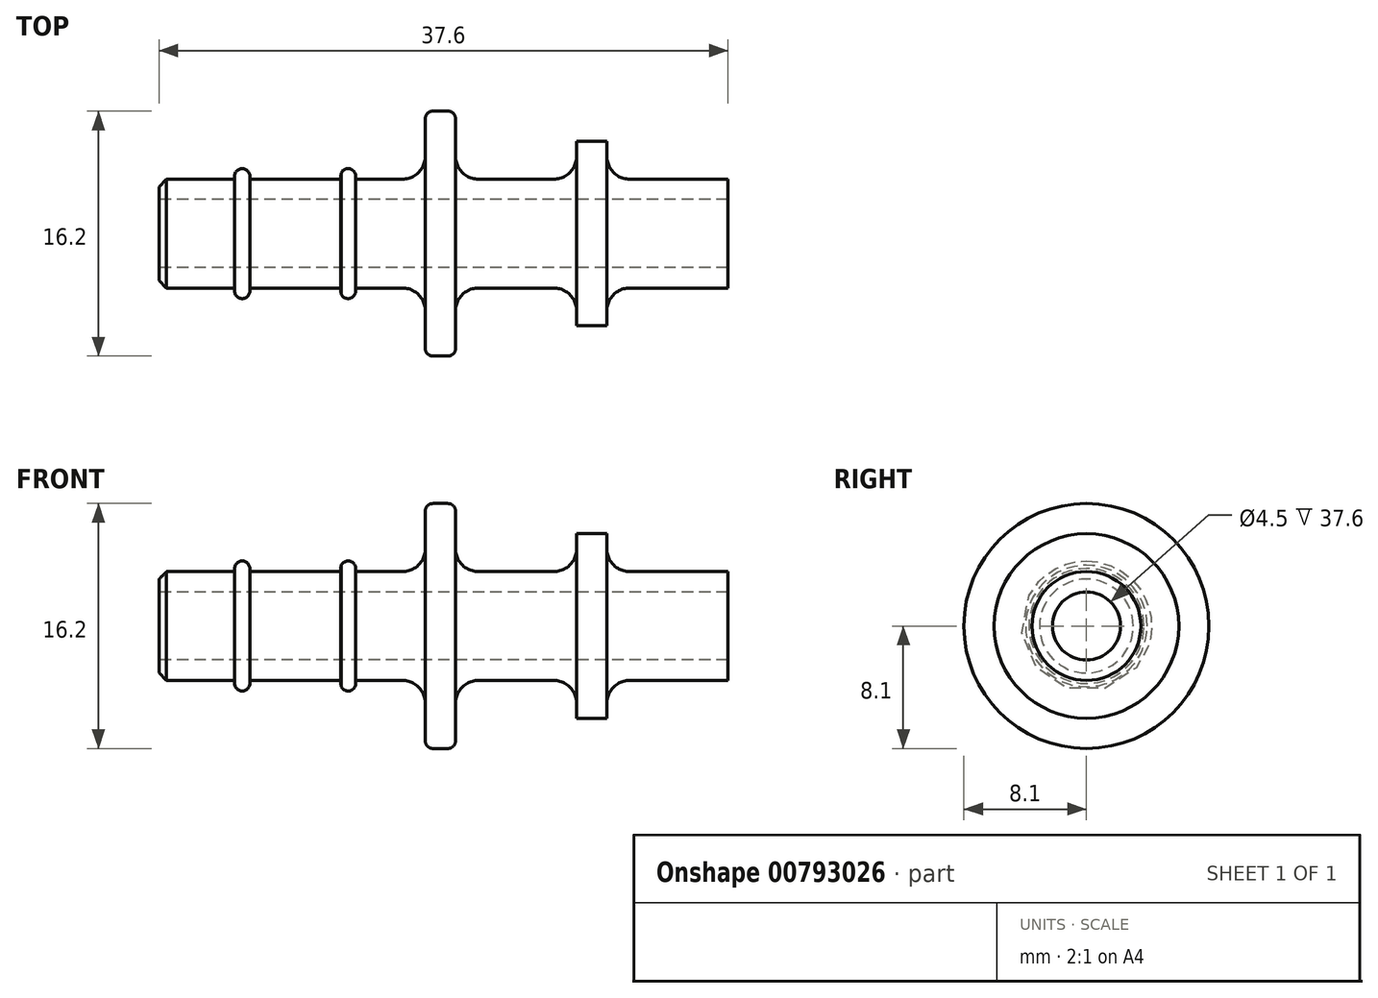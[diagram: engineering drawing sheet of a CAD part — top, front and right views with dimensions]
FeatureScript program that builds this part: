
annotation { "Feature Type Name" : "Feature", "Feature Type Description" : "" }
export const myFeature = defineFeature(function(context is Context, id is Id, definition is map)
    precondition{}
    {
        {
            var Q0;
            Q0=qCreatedBy(makeId("Front.planeOp"),FACE);
            var sketch = newSketch(context, id + "F0", { "sketchPlane" : qUnion([Q0])});
            skLineSegment(sketch, "E0.bottom", {"start": v(18.8, 0) * mm, "end": v(-18.8, 0) * mm});
            skLineSegment(sketch, "E0.top", {"start": v(-2.7, 3.6) * mm, "end": v(-18.8, 3.6) * mm});
            skLineSegment(sketch, "E0.left", {"start": v(18.8, 0) * mm, "end": v(18.8, 3.6) * mm});
            skLineSegment(sketch, "E0.right", {"start": v(-18.8, 0) * mm, "end": v(-18.8, 3.6) * mm});
            skPoint(sketch, "E0.middle", {"position": v(0, 1.8) * mm});
            skLineSegment(sketch, "E1", {"start": v(-19.54, 0) * mm, "end": v(19.6, 0) * mm, "construction": true});
            skLineSegment(sketch, "E2", {"start": v(10.8, 5.1) * mm, "end": v(10.8, 6.1) * mm});
            skLineSegment(sketch, "E3", {"start": v(10.8, 6.1) * mm, "end": v(8.8, 6.1) * mm});
            skLineSegment(sketch, "E4", {"start": v(8.8, 6.1) * mm, "end": v(8.8, 5.1) * mm});
            skLineSegment(sketch, "E5", {"start": v(0.8, 5.1) * mm, "end": v(0.8, 7.6) * mm});
            skLineSegment(sketch, "E6", {"start": v(0.3, 8.1) * mm, "end": v(-0.7, 8.1) * mm});
            skLineSegment(sketch, "E7", {"start": v(-1.2, 7.6) * mm, "end": v(-1.2, 5.1) * mm});
            skLineSegment(sketch, "E8", {"start": v(-5.8, 3.6) * mm, "end": v(-5.8, 3.8) * mm});
            skLineSegment(sketch, "E9", {"start": v(-6.8, 3.8) * mm, "end": v(-6.8, 3.6) * mm});
            skLineSegment(sketch, "E10", {"start": v(-12.8, 3.6) * mm, "end": v(-12.8, 3.8) * mm});
            skLineSegment(sketch, "E11", {"start": v(-13.8, 3.8) * mm, "end": v(-13.8, 3.6) * mm});
            skPoint(sketch, "E12.newPointB", {"position": v(18.8, 3.6) * mm});
            skArc(sketch, "E12.filletArc", {"start": v(-2.7, 3.6) * mm, "mid": v(-1.64, 4.04) * mm, "end": v(-1.2, 5.1) * mm});
            skLineSegment(sketch, "E13", {"start": v(2.3, 3.6) * mm, "end": v(7.3, 3.6) * mm});
            skLineSegment(sketch, "E14", {"start": v(12.3, 3.6) * mm, "end": v(18.8, 3.6) * mm});
            skPoint(sketch, "E15.visualSharp", {"position": v(0.8, 3.6) * mm});
            skArc(sketch, "E15.filletArc", {"start": v(0.8, 5.1) * mm, "mid": v(1.24, 4.04) * mm, "end": v(2.3, 3.6) * mm});
            skPoint(sketch, "E16.visualSharp", {"position": v(8.8, 3.6) * mm});
            skArc(sketch, "E16.filletArc", {"start": v(7.3, 3.6) * mm, "mid": v(8.36, 4.04) * mm, "end": v(8.8, 5.1) * mm});
            skPoint(sketch, "E17.visualSharp", {"position": v(10.8, 3.6) * mm});
            skArc(sketch, "E17.filletArc", {"start": v(10.8, 5.1) * mm, "mid": v(11.24, 4.04) * mm, "end": v(12.3, 3.6) * mm});
            skPoint(sketch, "E18.visualSharp", {"position": v(-1.2, 8.1) * mm});
            skArc(sketch, "E18.filletArc", {"start": v(-0.7, 8.1) * mm, "mid": v(-1.05, 7.95) * mm, "end": v(-1.2, 7.6) * mm});
            skPoint(sketch, "E19.visualSharp", {"position": v(0.8, 8.1) * mm});
            skArc(sketch, "E19.filletArc", {"start": v(0.8, 7.6) * mm, "mid": v(0.65, 7.95) * mm, "end": v(0.3, 8.1) * mm});
            skArc(sketch, "E20", {"start": v(-12.8, 3.8) * mm, "mid": v(-13.3, 4.3) * mm, "end": v(-13.8, 3.8) * mm});
            skLineSegment(sketch, "E21", {"start": v(-13.8, 3.8) * mm, "end": v(-13.8, 3.8) * mm});
            skLineSegment(sketch, "E22", {"start": v(-6.8, 3.8) * mm, "end": v(-6.72, 4.13) * mm});
            skArc(sketch, "E23", {"start": v(-6.8, 3.8) * mm, "mid": v(-6.3, 4.3) * mm, "end": v(-5.8, 3.8) * mm});
            skSolve(sketch);
        }
        {
            var Q0;
            Q0=makeQuery(id+"F0.imprint","IMPRINT",FACE,{"disambiguationData":[TD([[makeQuery(id+"F0.imprint","IMPRINT",EDGE,{"derivedFrom":sQuery(id+"F0.wireOp",EDGE,"E0.bottom")}),-1.0]])]});
            var Q1;
            {var subQ4=sQuery(id+"F0.wireOp",EDGE,"E8");Q1=makeQuery(id+"F0.imprint","IMPRINT",FACE,{"disambiguationData":[TD([[makeQuery(id+"F0.imprint","IMPRINT",EDGE,{"derivedFrom":subQ4}),1.0]])]});}
            var Q2;
            {var subQ1=sQuery(id+"F0.wireOp",EDGE,"E10");Q2=makeQuery(id+"F0.imprint","IMPRINT",FACE,{"disambiguationData":[TD([[makeQuery(id+"F0.imprint","IMPRINT",EDGE,{"derivedFrom":subQ1}),1.0]])]});}
            var Q3;
            Q3=sQuery(id+"F0.wireOp",EDGE,"E1");
            revolve(context, id + "F1", {"surfaceOperationType" : NewSurfaceOperationType.NEW, "entities" : qUnion([Q0, Q1, Q2]), "axis" : qUnion([Q3]), "revolveType" : RevolveType.FULL});
        }
        {
            var Q0;
            Q0=makeQuery(id+"F1.opRevolve","SWEPT_EDGE",EDGE,{"disambiguationData":[OSD([sQuery(id+"F0.wireOp",EDGE,"E0.top"),sQuery(id+"F0.wireOp",EDGE,"E0.right")])]});
            chamfer(context, id + "F2", {"entities" : qUnion([Q0]), "width" : 0.5 * mm, "tangentPropagation" : true});
        }
        {
            var Q0;
            Q0=makeQuery(id+"F1.opRevolve","SWEPT_FACE",FACE,{"disambiguationData":[OSD([sQuery(id+"F0.wireOp",EDGE,"E0.right")])]});
            var sketch = newSketch(context, id + "F3", { "sketchPlane" : qUnion([Q0])});
            skCircle(sketch, "E24", {"center": v(0, 0) * mm, "radius": 2.25 * mm});
            skSolve(sketch);
        }
        {
            var Q0;
            Q0=makeQuery(id+"F3.imprint","IMPRINT",FACE,{"disambiguationData":[TD([[makeQuery(id+"F3.imprint","IMPRINT",EDGE,{"derivedFrom":sQuery(id+"F3.wireOp",EDGE,"E24")}),1.0]])]});
            extrude(context, id + "F4", {"entities" : qUnion([Q0]), "operationType" : NewBodyOperationType.REMOVE, "endBound" : BoundingType.THROUGH_ALL, "oppositeDirection" : true, "depth" : 25 * mm, "offsetDistance" : 25 * mm});
        }
    });
